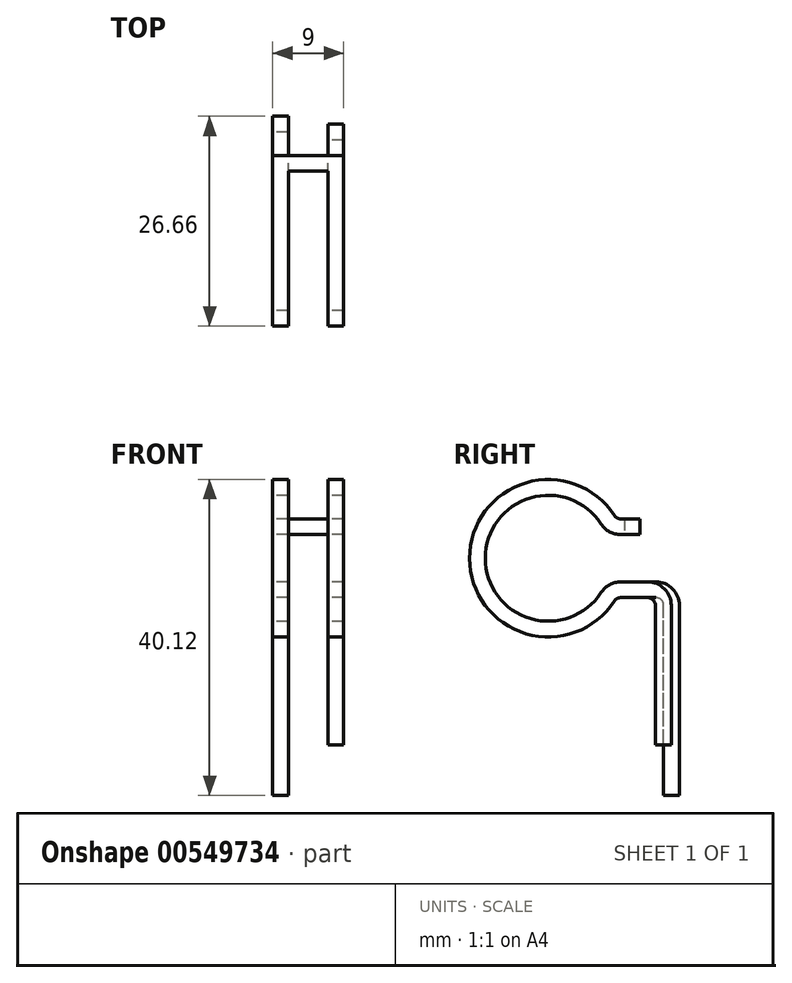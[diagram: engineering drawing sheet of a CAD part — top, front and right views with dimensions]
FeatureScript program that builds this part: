
annotation { "Feature Type Name" : "Feature", "Feature Type Description" : "" }
export const myFeature = defineFeature(function(context is Context, id is Id, definition is map)
    precondition{}
    {
        {
            var Q0;
            Q0=qCreatedBy(makeId("Right.planeOp"),FACE);
            var sketch = newSketch(context, id + "F0", { "sketchPlane" : qUnion([Q0])});
            skArc(sketch, "E0", {"start": v(8.38, 5.45) * mm, "mid": v(-10, 0) * mm, "end": v(8.38, -5.45) * mm});
            skLineSegment(sketch, "E1", {"start": v(9.22, -5) * mm, "end": v(13.66, -5) * mm});
            skLineSegment(sketch, "E2", {"start": v(14.66, -30.12) * mm, "end": v(14.66, -6) * mm});
            skPoint(sketch, "E3.orphan", {"position": v(55.45, -5) * mm});
            skLineSegment(sketch, "E4", {"start": v(9.22, 5) * mm, "end": v(11.66, 5) * mm});
            skPoint(sketch, "E5.visualSharp", {"position": v(14.66, -5) * mm});
            skArc(sketch, "E5.filletArc", {"start": v(14.66, -6) * mm, "mid": v(14.37, -5.3) * mm, "end": v(13.66, -5) * mm});
            skPoint(sketch, "E6.visualSharp", {"position": v(8.66, -5) * mm});
            skArc(sketch, "E6.filletArc", {"start": v(9.22, -5) * mm, "mid": v(8.74, -5.12) * mm, "end": v(8.38, -5.45) * mm});
            skPoint(sketch, "E7.visualSharp", {"position": v(8.66, 5) * mm});
            skArc(sketch, "E7.filletArc", {"start": v(8.38, 5.45) * mm, "mid": v(8.74, 5.12) * mm, "end": v(9.22, 5) * mm});
            skLineSegment(sketch, "E8.0", {"start": v(9.22, 3) * mm, "end": v(11.66, 3) * mm});
            skArc(sketch, "E8.1", {"start": v(6.7, 4.36) * mm, "mid": v(7.79, 3.36) * mm, "end": v(9.22, 3) * mm});
            skArc(sketch, "E8.2", {"start": v(6.7, 4.36) * mm, "mid": v(-8, 0) * mm, "end": v(6.7, -4.36) * mm});
            skLineSegment(sketch, "E8.3", {"start": v(16.66, -30.12) * mm, "end": v(16.66, -6) * mm});
            skArc(sketch, "E8.4", {"start": v(16.66, -6) * mm, "mid": v(15.78, -3.88) * mm, "end": v(13.66, -3) * mm});
            skLineSegment(sketch, "E8.5", {"start": v(9.22, -3) * mm, "end": v(13.66, -3) * mm});
            skArc(sketch, "E8.6", {"start": v(9.22, -3) * mm, "mid": v(7.79, -3.36) * mm, "end": v(6.7, -4.36) * mm});
            skLineSegment(sketch, "E9", {"start": v(16.66, -30.12) * mm, "end": v(14.66, -30.12) * mm});
            skLineSegment(sketch, "E10", {"start": v(11.66, 3) * mm, "end": v(11.66, 5) * mm});
            skSolve(sketch);
        }
        {
            var Q0;
            Q0 = qSketchRegion(id + "F0", true);
            extrude(context, id + "F1", {"entities" : qUnion([Q0]), "depth" : 2 * mm, "offsetDistance" : 25 * mm});
        }
        {
            var Q0;
            Q0=makeQuery(id+"F1.opExtrude","CAP_FACE",FACE,{"disambiguationData":[OSD([sQuery(id+"F0.wireOp",EDGE,"E0"),sQuery(id+"F0.wireOp",EDGE,"E1"),sQuery(id+"F0.wireOp",EDGE,"E2"),sQuery(id+"F0.wireOp",EDGE,"E4"),sQuery(id+"F0.wireOp",EDGE,"E5.filletArc"),sQuery(id+"F0.wireOp",EDGE,"E6.filletArc"),sQuery(id+"F0.wireOp",EDGE,"E7.filletArc"),sQuery(id+"F0.wireOp",EDGE,"E8.0"),sQuery(id+"F0.wireOp",EDGE,"E8.1"),sQuery(id+"F0.wireOp",EDGE,"E8.2"),sQuery(id+"F0.wireOp",EDGE,"E8.3"),sQuery(id+"F0.wireOp",EDGE,"E8.4"),sQuery(id+"F0.wireOp",EDGE,"E8.5"),sQuery(id+"F0.wireOp",EDGE,"E8.6"),sQuery(id+"F0.wireOp",EDGE,"E9"),sQuery(id+"F0.wireOp",EDGE,"E10")])],"isStart":false});
            var sketch = newSketch(context, id + "F2", { "sketchPlane" : qUnion([Q0])});
            skLineSegment(sketch, "E11.bottom", {"start": v(11.66, 5) * mm, "end": v(9.66, 5) * mm});
            skLineSegment(sketch, "E11.top", {"start": v(11.66, 3) * mm, "end": v(9.66, 3) * mm});
            skLineSegment(sketch, "E11.left", {"start": v(11.66, 5) * mm, "end": v(11.66, 3) * mm});
            skLineSegment(sketch, "E11.right", {"start": v(9.66, 5) * mm, "end": v(9.66, 3) * mm});
            skSolve(sketch);
        }
        {
            var Q0;
            Q0 = qSketchRegion(id + "F2", true);
            extrude(context, id + "F3", {"entities" : qUnion([Q0]), "operationType" : NewBodyOperationType.ADD, "depth" : 5 * mm, "offsetDistance" : 25 * mm});
        }
        {
            var Q0;
            Q0=makeQuery(id+"F3.opExtrude","CAP_FACE",FACE,{"disambiguationData":[OSD([sQuery(id+"F2.wireOp",EDGE,"E11.bottom"),sQuery(id+"F2.wireOp",EDGE,"E11.top"),sQuery(id+"F2.wireOp",EDGE,"E11.left"),sQuery(id+"F2.wireOp",EDGE,"E11.right")])],"isStart":false});
            var sketch = newSketch(context, id + "F4", { "sketchPlane" : qUnion([Q0])});
            skArc(sketch, "E12", {"start": v(8.38, 5.45) * mm, "mid": v(-10, 0) * mm, "end": v(8.38, -5.45) * mm});
            skLineSegment(sketch, "E13", {"start": v(9.22, -5) * mm, "end": v(12.62, -5) * mm});
            skLineSegment(sketch, "E14", {"start": v(13.62, -23.69) * mm, "end": v(13.62, -6) * mm});
            skPoint(sketch, "E15.orphan", {"position": v(55.45, -5) * mm});
            skLineSegment(sketch, "E16", {"start": v(9.22, 5) * mm, "end": v(11.66, 5) * mm});
            skPoint(sketch, "E17.visualSharp", {"position": v(13.62, -5) * mm});
            skArc(sketch, "E17.filletArc", {"start": v(13.62, -6) * mm, "mid": v(13.33, -5.3) * mm, "end": v(12.62, -5) * mm});
            skPoint(sketch, "E18.visualSharp", {"position": v(8.66, -5) * mm});
            skArc(sketch, "E18.filletArc", {"start": v(9.22, -5) * mm, "mid": v(8.74, -5.12) * mm, "end": v(8.38, -5.45) * mm});
            skPoint(sketch, "E19.visualSharp", {"position": v(8.66, 5) * mm});
            skArc(sketch, "E19.filletArc", {"start": v(8.38, 5.45) * mm, "mid": v(8.74, 5.12) * mm, "end": v(9.22, 5) * mm});
            skLineSegment(sketch, "E20.0", {"start": v(9.22, 3) * mm, "end": v(11.66, 3) * mm});
            skArc(sketch, "E20.1", {"start": v(6.7, 4.36) * mm, "mid": v(7.79, 3.36) * mm, "end": v(9.22, 3) * mm});
            skArc(sketch, "E20.2", {"start": v(6.7, 4.36) * mm, "mid": v(-8, 0) * mm, "end": v(6.7, -4.36) * mm});
            skLineSegment(sketch, "E20.3", {"start": v(15.62, -23.69) * mm, "end": v(15.62, -6) * mm});
            skArc(sketch, "E20.4", {"start": v(15.62, -6) * mm, "mid": v(14.74, -3.88) * mm, "end": v(12.62, -3) * mm});
            skLineSegment(sketch, "E20.5", {"start": v(9.22, -3) * mm, "end": v(12.62, -3) * mm});
            skArc(sketch, "E20.6", {"start": v(9.22, -3) * mm, "mid": v(7.79, -3.36) * mm, "end": v(6.7, -4.36) * mm});
            skLineSegment(sketch, "E21", {"start": v(15.62, -23.69) * mm, "end": v(13.62, -23.69) * mm});
            skLineSegment(sketch, "E22", {"start": v(11.66, 3) * mm, "end": v(11.66, 5) * mm});
            skSolve(sketch);
        }
        {
            var Q0;
            Q0 = qSketchRegion(id + "F4", true);
            extrude(context, id + "F5", {"entities" : qUnion([Q0]), "operationType" : NewBodyOperationType.ADD, "depth" : 2 * mm, "offsetDistance" : 25 * mm});
        }
    });
